# Revit family: ISO Family
name_source: partatom
category: Furniture
revit_build: Autodesk Revit 2018 (Build: 20170223_1515(x64)
units: mm (PartAtom-declared; Revit-internal decimal feet)

## family parameters
Always vertical = Yes
Cut with Voids When Loaded = No
OmniClass Number = 23.40.20.00
OmniClass Title = General Furniture and Specialties
Room Calculation Point = No
Shared = No
Work Plane-Based = No

## types (8) — shared parameters

## per-type parameters (varying)
| type | FurnitureType |
| Table for 4 (1500X750X730) | ISO Range Family : Table for 4 (1500X750) |
| Table for 6 (1800X1000X730) | ISO Range Family : Table for 6 (1800X1000) |
| Table for 6-8 (2000X1000X730) | ISO Range Family : Table for 6-8 (2000X1000) |
| Table for 8 (2400X1000X730) | ISO Range Family : Table for 8 (2400X1000) |
| Table for 4-8 (1200X1200X730) | ISO Range Family : Table for 4-8 (1200X1200) |
| Table for 8-10 (2000X1200X730) | ISO Range Family : Table for 8-10 (2000X1200) |
| Table for 8-12 (2400X1200X730) | ISO Range Family : Table for 8-12 (2400X1200) |
| Table for 10-14 (2800X1200X730) | ISO Range Family : Table for 10-14 (2800X1200) |

## geometry (parser evidence)
native form markers: Blend x6, Sweep x74
no freeform markers — native parametric forms only
